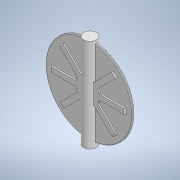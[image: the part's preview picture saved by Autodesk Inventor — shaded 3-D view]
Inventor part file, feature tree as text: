
AUTODESK INVENTOR PART (.ipt)
format: ipt  version: 2020.2 (Build 242310000, 310)  size: 286,720 bytes
history: native  units: mm
features: extrude x4, sketch x4, chamfer x1, mirror x1, fillet x1
ambient origin geometry x8: Origin, YZ Plane, XZ Plane, XY Plane, X Axis, Y Axis, Z Axis, Center Point
bodies: Solid1 (feature_tree)
feature tree (11):
  extrude  "Extrusion1"  Depth=5.0mm TaperAngle=0.0deg
  extrude  "Extrusion2"  Depth=109.5mm TaperAngle=0.0deg
  extrude  "Extrusion3"  Depth=60.0mm
  chamfer  "Chamfer1"  Angle=360.0deg  [1 undecoded]
  mirror  "Mirror2"
  fillet  "Fillet2"  Radius=3.0mm
  extrude  "Extrusion5"  Depth=15.0mm
  sketch  "Sketch1"  dims[d0=200.0mm d1=5.0mm d2=0.0mm]
  sketch  "Sketch2"  dims[d3=29.6mm d4=105.5mm d5=109.5mm d6=0.0mm d7=0.0mm]
  sketch  "Sketch3"  dims[d10=6.0mm d12=60.0mm]
  sketch  "Sketch6"  dims[d13=3.454961mm d16=360.0deg d18=3.0mm d19=0.0mm d23=5.0mm d24=2.5mm d25=0.0mm d26=3.0mm d27=2.0mm d28=45.0deg d29=1.5mm d33=0.2mm d34=15.0mm d35=0.0mm]
note: 1 required parameter value undecoded (feature->parameter linkage not recoverable at this tier; creation-order binding heuristic only, values carry confidence <= 0.55)
